# Revit family: xxxDrinking_Fountain-Bottle_Filler-Wall_Mounted-Murdock_Mfg-A171-UG-VR-D1-BF_Series
name_source: partatom
category: Plumbing Fixtures
units: mm (PartAtom-declared; Revit-internal decimal feet)

## family parameters
Cut with Voids When Loaded = Yes
Host = Face
OmniClass Number = 23.65.70.14.11
OmniClass Title = Drinking Fountains/Coolers
Part Type = Normal
Room Calculation Point = No
Round Connector Dimension = Use Diameter
Shared = Yes

## types (2) — shared parameters
-BF1S Bottle Filler with PushButton Operation = Yes
-BF2S Bottle Filler with Sensor Operation = No
-BF2S-BAT Bottle Filler with Battery Operated Sensor Operation = No
-BF2S-BCD Bottle Filler with Sensor Operation with Bottle Counter Display = No
-CSC5 Concealed Support Carrier = No
-DD Drop Down Door = No
-LOGO Customer Specified Logo / Graphics = No
-WF1 1500-Gallon Capacity, NSF 42+53, 1-Micron Lead Reduction Filter = No
-WF3 3000-Gallon Capacity, NSF 42+53, 1-Micron Lead Reduction Filter = No
115VAC Plug-In Transformer = No
ADA Compliant = Yes
Activation = Push Button or Sensor Operated
Assembly Code = D2010820
Bubbler Height A.F.F. = 33"
CW Connection = Yes
CWFU = 1.5
Cold Water Connection Diameter = 3/8"
Cold Water Connection Height = 19 3/8"
Cold Water Connection Width = 2"
Default Elevation = 0"
Description = Barrier-Free Wall Mount Drinking Fountain with Vandal-Resistant Push Button and Heavy Duty Bottle Filler - No Refrigeration
Finish = Stainless Steel-Murdock-Type 304-Satin
Finish- Bottle Filler Housing = Stainless Steel-Murdock-Satin
Finish- Others = Plastic-Murdock-Black
Finish- Push Button = Brass-Murdock-Chrome Plated
Flow Rate = 1.00 GPM
HW Connection = No
Height = 47 5/8"
Height From Floor Level = 30 5/8"
Height- Bottle Filler Sensor = 40 7/8"
IAPMO Compliance = NSF/ANSI 61 & Federal Public Law 111-380 (No lead)
Installation Instruction Link = https://www.murdockmfg.com
Installation Type = Wall Mounted
Laminar (LAM) = Yes
Length = 18 1/2"
Manufacturer = Murdock Manufacturing
Material = Stainless Steel-Murdock-Type 304-Satin
Price = Prices may vary. Please consult Manufacturer Representative for most up-to-date price list.
Product Documentation Link = https://www.murdockmfg.com
Product Page URL = https://www.murdockmfg.com
Revised Date = 07/19/2022
Sensor Operated = No
URL = https://www.murdockmfg.com
Vent Connection = No
Voltage Nominal = 0 V
WFU = 2
Waste Connection = Yes
Waste Connection Diameter = 1 1/4"
Waste Connection Height = 22 1/4"
Water Pressure = 20-105 PSIG
Width = 18 1/2"
cUPC Compliant = Yes
zero-valued in all types: HWFU

## per-type parameters (varying)
| type | Finish- Bubbler |
| A171400S-UG-VR-D1 | Stainless Steel-Murdock-Satin |
| A171400F-UG-VR-D1 | Stainless Steel-Murdock-Satin-Flexible |

note: column(s) folded — value = type name in every type: Model

## geometry (parser evidence)
native form markers: Sweep x3
no freeform markers — native parametric forms only
